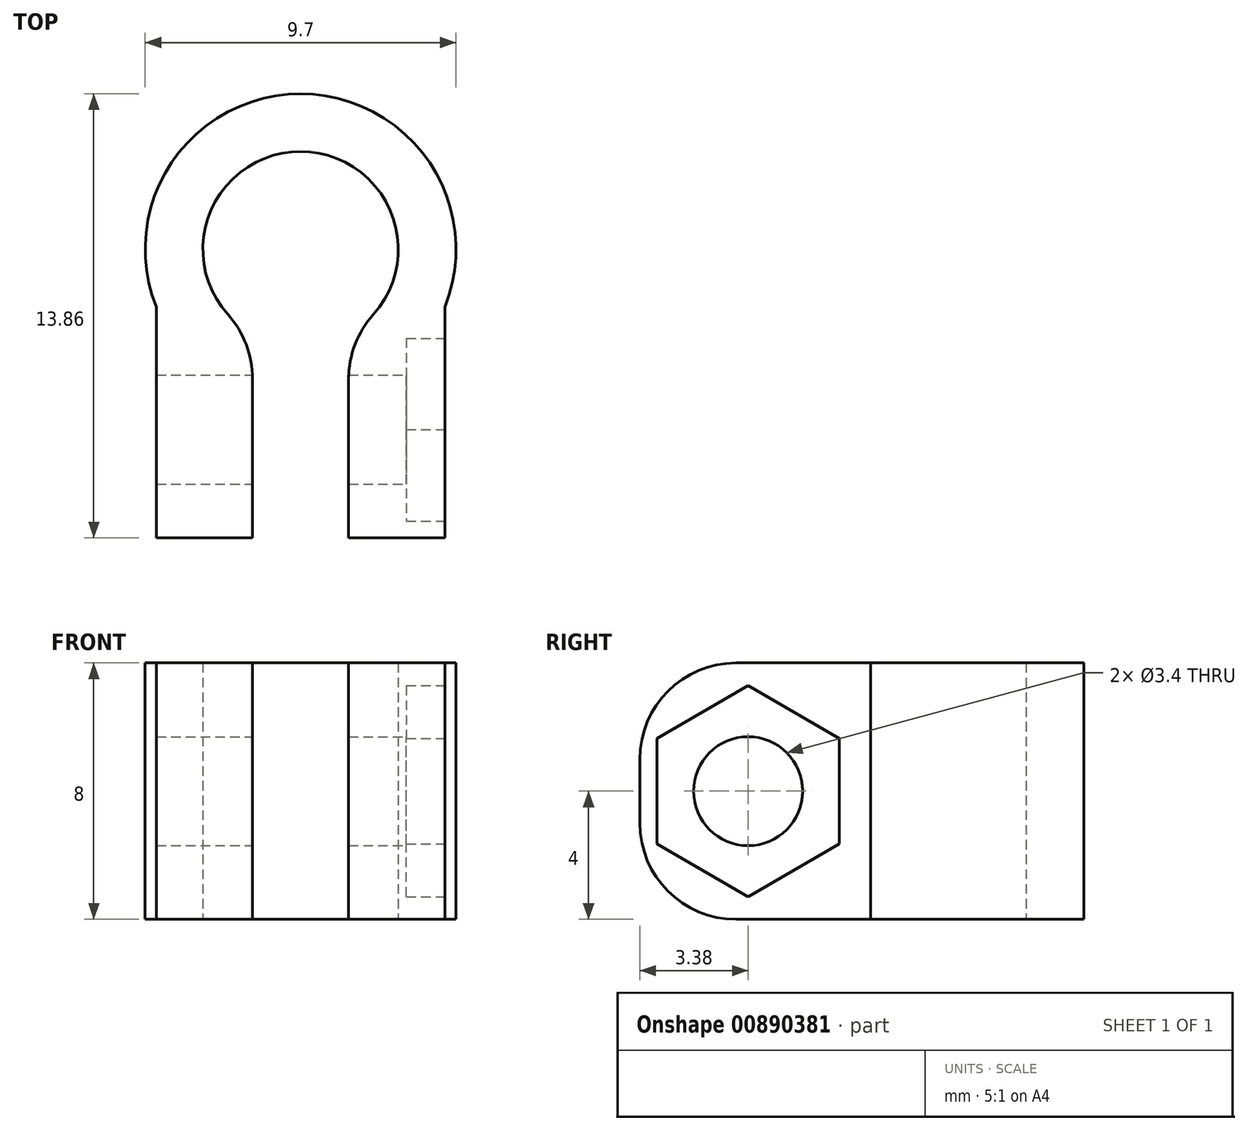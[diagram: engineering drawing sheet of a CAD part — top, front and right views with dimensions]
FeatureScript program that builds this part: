
annotation { "Feature Type Name" : "Feature", "Feature Type Description" : "" }
export const myFeature = defineFeature(function(context is Context, id is Id, definition is map)
    precondition{}
    {
        {
            var Q0;
            Q0=qCreatedBy(makeId("Top.planeOp"),FACE);
            var sketch = newSketch(context, id + "F0", { "sketchPlane" : qUnion([Q0])});
            skCircle(sketch, "E0", {"center": v(0, 0) * mm, "radius": 3.05 * mm});
            skCircle(sketch, "E1", {"center": v(0, 0) * mm, "radius": 4.85 * mm});
            skLineSegment(sketch, "E2.bottom", {"start": v(-4.5, -1.8) * mm, "end": v(4.5, -1.8) * mm});
            skLineSegment(sketch, "E2.top", {"start": v(-4.5, -9) * mm, "end": v(4.5, -9) * mm});
            skLineSegment(sketch, "E2.left", {"start": v(-4.5, -1.8) * mm, "end": v(-4.5, -9) * mm});
            skLineSegment(sketch, "E2.right", {"start": v(4.5, -1.8) * mm, "end": v(4.5, -9) * mm});
            skLineSegment(sketch, "E3.bottom", {"start": v(-1.5, -2.66) * mm, "end": v(1.5, -2.66) * mm});
            skLineSegment(sketch, "E3.top", {"start": v(-1.5, -9) * mm, "end": v(1.5, -9) * mm});
            skLineSegment(sketch, "E3.left", {"start": v(-1.5, -2.66) * mm, "end": v(-1.5, -9) * mm});
            skLineSegment(sketch, "E3.right", {"start": v(1.5, -2.66) * mm, "end": v(1.5, -9) * mm});
            skSolve(sketch);
        }
        {
            var Q0;
            {var subQ1=sQuery(id+"F0.wireOp",EDGE,"E1");var subQ3=sQuery(id+"F0.wireOp",EDGE,"E3.left");var subQ4=makeQuery(id+"F0.imprint","INTERSECT",VERTEX,{"derivedFrom":[subQ1,subQ3]});Q0=makeQuery(id+"F0.imprint","IMPRINT",FACE,{"disambiguationData":[TD([[makeQuery(id+"F0.imprint","IMPRINT",EDGE,{"disambiguationData":[TD([[subQ4,1.0]])],"derivedFrom":subQ3}),-1.0]])]});}
            var Q1;
            {var subQ1=sQuery(id+"F0.wireOp",EDGE,"E1");var subQ3=sQuery(id+"F0.wireOp",EDGE,"E3.right");var subQ4=makeQuery(id+"F0.imprint","INTERSECT",VERTEX,{"derivedFrom":[subQ1,subQ3]});Q1=makeQuery(id+"F0.imprint","IMPRINT",FACE,{"disambiguationData":[TD([[makeQuery(id+"F0.imprint","IMPRINT",EDGE,{"disambiguationData":[TD([[subQ4,1.0]])],"derivedFrom":subQ3}),1.0]])]});}
            var Q2;
            {var subQ0=sQuery(id+"F0.wireOp",EDGE,"E2.right");Q2=makeQuery(id+"F0.imprint","IMPRINT",FACE,{"disambiguationData":[TD([[makeQuery(id+"F0.imprint","IMPRINT",EDGE,{"derivedFrom":subQ0}),-1.0]])]});}
            var Q3;
            {var subQ0=sQuery(id+"F0.wireOp",EDGE,"E2.left");Q3=makeQuery(id+"F0.imprint","IMPRINT",FACE,{"disambiguationData":[TD([[makeQuery(id+"F0.imprint","IMPRINT",EDGE,{"derivedFrom":subQ0}),1.0]])]});}
            var Q4;
            {var subQ0=sQuery(id+"F0.wireOp",EDGE,"E2.bottom");var subQ1=sQuery(id+"F0.wireOp",EDGE,"E0");var subQ2=makeQuery(id+"F0.imprint","INTERSECT",VERTEX,{"disambiguationData":[OD(0.0)],"derivedFrom":[subQ1,subQ0]});Q4=makeQuery(id+"F0.imprint","IMPRINT",FACE,{"disambiguationData":[TD([[makeQuery(id+"F0.imprint","IMPRINT",EDGE,{"disambiguationData":[TD([[subQ2,1.0]])],"derivedFrom":subQ1}),-1.0]])]});}
            extrude(context, id + "F1", {"entities" : qUnion([Q0, Q1, Q2, Q3, Q4]), "depth" : 8 * mm, "offsetDistance" : 25 * mm});
        }
        {
            var Q0;
            Q0=makeQuery(id+"F1.opExtrude","SWEPT_FACE",FACE,{"disambiguationData":[OSD([sQuery(id+"F0.wireOp",EDGE,"E2.right")])]});
            var sketch = newSketch(context, id + "F2", { "sketchPlane" : qUnion([Q0])});
            skCircle(sketch, "E4", {"center": v(-5.63, 4) * mm, "radius": 1.7 * mm});
            skPoint(sketch, "E4.centerSnap0", {"position": v(-9, 4) * mm});
            skCircle(sketch, "E5.cCircle", {"center": v(-5.63, 4) * mm, "radius": 2.85 * mm, "construction": true});
            skLineSegment(sketch, "E5.0", {"start": v(-8.48, 2.35) * mm, "end": v(-8.48, 5.65) * mm});
            skLineSegment(sketch, "E5.1", {"start": v(-8.48, 5.65) * mm, "end": v(-5.63, 7.3) * mm});
            skLineSegment(sketch, "E5.2", {"start": v(-5.63, 7.3) * mm, "end": v(-2.78, 5.65) * mm});
            skLineSegment(sketch, "E5.3", {"start": v(-2.78, 5.65) * mm, "end": v(-2.78, 2.35) * mm});
            skLineSegment(sketch, "E5.4", {"start": v(-2.78, 2.35) * mm, "end": v(-5.63, 0.7) * mm});
            skLineSegment(sketch, "E5.5", {"start": v(-5.63, 0.7) * mm, "end": v(-8.48, 2.35) * mm});
            skPoint(sketch, "E5.0.midPoint", {"position": v(-8.48, 4) * mm});
            skCircle(sketch, "E6", {"center": v(-5.63, 4) * mm, "radius": 2.75 * mm});
            skSolve(sketch);
        }
        {
            var Q0;
            Q0=makeQuery(id+"F2.imprint","IMPRINT",FACE,{"disambiguationData":[TD([[makeQuery(id+"F2.imprint","IMPRINT",EDGE,{"derivedFrom":sQuery(id+"F2.wireOp",EDGE,"E4")}),1.0]])]});
            extrude(context, id + "F3", {"entities" : qUnion([Q0]), "operationType" : NewBodyOperationType.REMOVE, "endBound" : BoundingType.THROUGH_ALL, "oppositeDirection" : true, "depth" : 25 * mm, "offsetDistance" : 25 * mm});
        }
        {
            var Q0;
            Q0=makeQuery(id+"F2.imprint","IMPRINT",FACE,{"disambiguationData":[TD([[makeQuery(id+"F2.imprint","IMPRINT",EDGE,{"derivedFrom":sQuery(id+"F2.wireOp",EDGE,"E5.0")}),-1.0]])]});
            var Q1;
            Q1=makeQuery(id+"F2.imprint","IMPRINT",FACE,{"disambiguationData":[TD([[makeQuery(id+"F2.imprint","IMPRINT",EDGE,{"derivedFrom":sQuery(id+"F2.wireOp",EDGE,"E4")}),-1.0]])]});
            extrude(context, id + "F4", {"entities" : qUnion([Q0, Q1]), "operationType" : NewBodyOperationType.REMOVE, "oppositeDirection" : true, "depth" : 1.2 * mm, "offsetDistance" : 25 * mm});
        }
        {
            var Q0;
            Q0=makeQuery(id+"F1.opExtrude","SWEPT_EDGE",EDGE,{"disambiguationData":[OSD([sQuery(id+"F0.wireOp",EDGE,"E0"),sQuery(id+"F0.wireOp",EDGE,"E3.bottom"),sQuery(id+"F0.wireOp",EDGE,"E3.right")])]});
            var Q1;
            Q1=makeQuery(id+"F1.opExtrude","SWEPT_EDGE",EDGE,{"disambiguationData":[OSD([sQuery(id+"F0.wireOp",EDGE,"E0"),sQuery(id+"F0.wireOp",EDGE,"E3.bottom"),sQuery(id+"F0.wireOp",EDGE,"E3.left")])]});
            var Q2;
            {var subQ0=sQuery(id+"F0.wireOp",EDGE,"E2.top");Q2=makeQuery(id+"F1.opExtrude","CAP_EDGE",EDGE,{"disambiguationData":[OSD([subQ0]),TDD([makeQuery(id+"F0.imprint","IMPRINT",EDGE,{"disambiguationData":[TD([[makeQuery(id+"F0.imprint","INTERSECT",VERTEX,{"derivedFrom":[subQ0,sQuery(id+"F0.wireOp",EDGE,"E2.right")]}),1.0]])],"derivedFrom":subQ0})])],"isStart":false});}
            var Q3;
            {var subQ0=sQuery(id+"F0.wireOp",EDGE,"E2.top");Q3=makeQuery(id+"F1.opExtrude","CAP_EDGE",EDGE,{"disambiguationData":[OSD([subQ0]),TDD([makeQuery(id+"F0.imprint","IMPRINT",EDGE,{"disambiguationData":[TD([[makeQuery(id+"F0.imprint","INTERSECT",VERTEX,{"derivedFrom":[subQ0,sQuery(id+"F0.wireOp",EDGE,"E2.left")]}),-1.0]])],"derivedFrom":subQ0})])],"isStart":false});}
            var Q4;
            {var subQ0=sQuery(id+"F0.wireOp",EDGE,"E2.top");Q4=makeQuery(id+"F1.opExtrude","CAP_EDGE",EDGE,{"disambiguationData":[OSD([subQ0]),TDD([makeQuery(id+"F0.imprint","IMPRINT",EDGE,{"disambiguationData":[TD([[makeQuery(id+"F0.imprint","INTERSECT",VERTEX,{"derivedFrom":[subQ0,sQuery(id+"F0.wireOp",EDGE,"E2.right")]}),1.0]])],"derivedFrom":subQ0})])],"isStart":true});}
            var Q5;
            {var subQ0=sQuery(id+"F0.wireOp",EDGE,"E2.top");Q5=makeQuery(id+"F1.opExtrude","CAP_EDGE",EDGE,{"disambiguationData":[OSD([subQ0]),TDD([makeQuery(id+"F0.imprint","IMPRINT",EDGE,{"disambiguationData":[TD([[makeQuery(id+"F0.imprint","INTERSECT",VERTEX,{"derivedFrom":[subQ0,sQuery(id+"F0.wireOp",EDGE,"E2.left")]}),-1.0]])],"derivedFrom":subQ0})])],"isStart":true});}
            fillet(context, id + "F5", {"entities" : qUnion([Q0, Q1, Q2, Q3, Q4, Q5]), "radius" : 3 * mm, "tangentPropagation" : true, "allowEdgeOverflow" : false});
        }
    });
